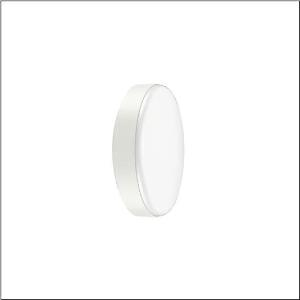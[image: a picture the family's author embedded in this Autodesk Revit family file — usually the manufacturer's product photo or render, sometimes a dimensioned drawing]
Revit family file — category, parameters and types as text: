
# Revit family: rondel_31_51wc10da32as
name_source: partatom
category: Lighting Fixtures
units: mm (PartAtom-declared; Revit-internal decimal feet)

## family parameters
Cut with Voids When Loaded = No
Host = Face
Light Source = No
Part Type = Normal
Room Calculation Point = No
Round Connector Dimension = Use Diameter
Shared = No

## types (1)
- Rondel 31 (1 x LED, 2450 lm, 20.4 W, 3000K)
    Apparent Load = 20 VA
    CIE Flux Codes = 44 75 94 94 100
    Color Rendering = 80
    Color Temperature = 3000K
    Default Elevation = 1800 mm
    Description = Rondel 31, wall and ceiling luminaire, primary optical cover: cover, of PC, opal, light emission: direct distribution, primary light characteristic: symmetric, installation type: surface-mounted, LED, rated luminous flux: 2.450lm, luminous efficacy: 120lm/W, light colour: 830, colour temperature: 3000K, with terminal, 5-pole, max. 2.5mm², mains connection: 220..240V, AC, 50/60Hz, rated input power: 20.5W, luminaire housing, of PC, traffic white (RAL 9016), diameter: 350mm, brightness and presence sensor, HF sensor, protection rating (complete): IP65, insulation class (complete): insulation class II (safety insulation), certification: CE, impact resistance: IK10, permissible operating ambient temperature: -20..+40°C, permissible storage temperature: -20..+60°C, packaging unit: 1 piece
    Height = 97 mm
    Lamp = 1 x LED
    Lamp Light Flux = 2450 lm
    Lamp Power = 20.4 W
    Lamp count = 1
    Length = 350 mm
    Luminous efficacy = 120 lm/W
    Manufacturer = Siteco
    ModVariant = No
    Model = 51WC10DA32AS
    Mounting Place = Ceiling
    Mounting Type = Surface mounted
    Number of Poles = 1
    OnlyDefault = Yes
    Power Factor = 1
    Product Name = Rondel 31
    Product group = wall and ceiling luminaire
    ProductGroupID = 302
    Protection Class = Protection class II
    Protection Degree = IP 65
    RLX_Detail_Level = 1
    RLX_Emergency_Light_Flux = 0 lm
    RLX_Emergency_Type = 0
    RLX_Emergency_Type_DB = No
    RlxData = <blob elided: 29605 chars, md5=235c4379>
    Socket = socket
    Standby Power = 0 W
    System Light Flux = 2450 lm
    System Power = 20 W
    Type Comments = Product without accessories
    Type Image = l_1007027.jpg
    URL = http://relux.com
    VarID = ---
    Voltage = 0 V
    Weight = 0.00 kg
    Width = 0 mm  [stored 0 ft]

note: [stored X ft] marks values corroborated as IEEE doubles in the binary element streams (Revit-internal decimal feet)

## geometry (parser evidence)
native form markers: Blend x4, Sweep x11
no freeform markers — native parametric forms only
